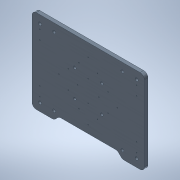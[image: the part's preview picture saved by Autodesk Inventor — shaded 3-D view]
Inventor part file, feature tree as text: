
AUTODESK INVENTOR PART (.ipt)
format: ipt  version: 2020.3 (Build 243373000, 373)  size: 216,576 bytes
history: native  units: in
note: dims shown in document units (in); Inventor stores cm internally (conversion verified against a paired STEP export)
features: hole x3, extrude x2, chamfer x1, fillet x1, sketch x1
ambient origin geometry x8: Origin, YZ Plane, XZ Plane, XY Plane, X Axis, Y Axis, Z Axis, Center Point
bodies: Solid1 (feature_tree)
feature tree (8):
  extrude  "Extrusion1"  Depth=14.75in
  hole  "Hole1"  [1 undecoded]
  extrude  "Extrusion2"  Depth=0.25in
  chamfer  "Chamfer1"  Distance=11.0in
  fillet  "Fillet1"  Radius=11.0in
  hole  "Hole3"  [1 undecoded]
  hole  "Hole4"  [1 undecoded]
  sketch  "Sketch3"  dims[d0=19.75in d1=14.75in d2=17.0in d3=12.0in d4=11.0in d5=11.0in d7=0.625in d8=0.0in d9=0.551in d10=0.625in d11=0.375in d12=0.25in d13=0.5635in d14=0.903in d15=0.8108in d16=0.75in d17=0.0in d18=0.0in d28=0.0in d29=0.875in d30=12.0in d31=1.0in d32=0.0in d33=0.875in d34=0.125in d35=45.0deg d36=3.5in d37=3.5in d38=1.902in d39=0.1628in d40=0.394in d41=0.375in d42=0.25in d43=0.5635in d44=0.559in d45=0.8108in d46=12.0in d47=12.0in d48=4.75in d49=4.75in d50=0.5in d51=0.75in d52=0.375in d53=0.25in d54=0.5635in d55=1.0in d56=0.8108in d57=3.25in d58=3.5in d59=3.5in d60=2.25in d61=3.875in d62=11.5in d63=9.875in d64=3.25in]
note: 3 required parameter values undecoded (feature->parameter linkage not recoverable at this tier; creation-order binding heuristic only, values carry confidence <= 0.55)
